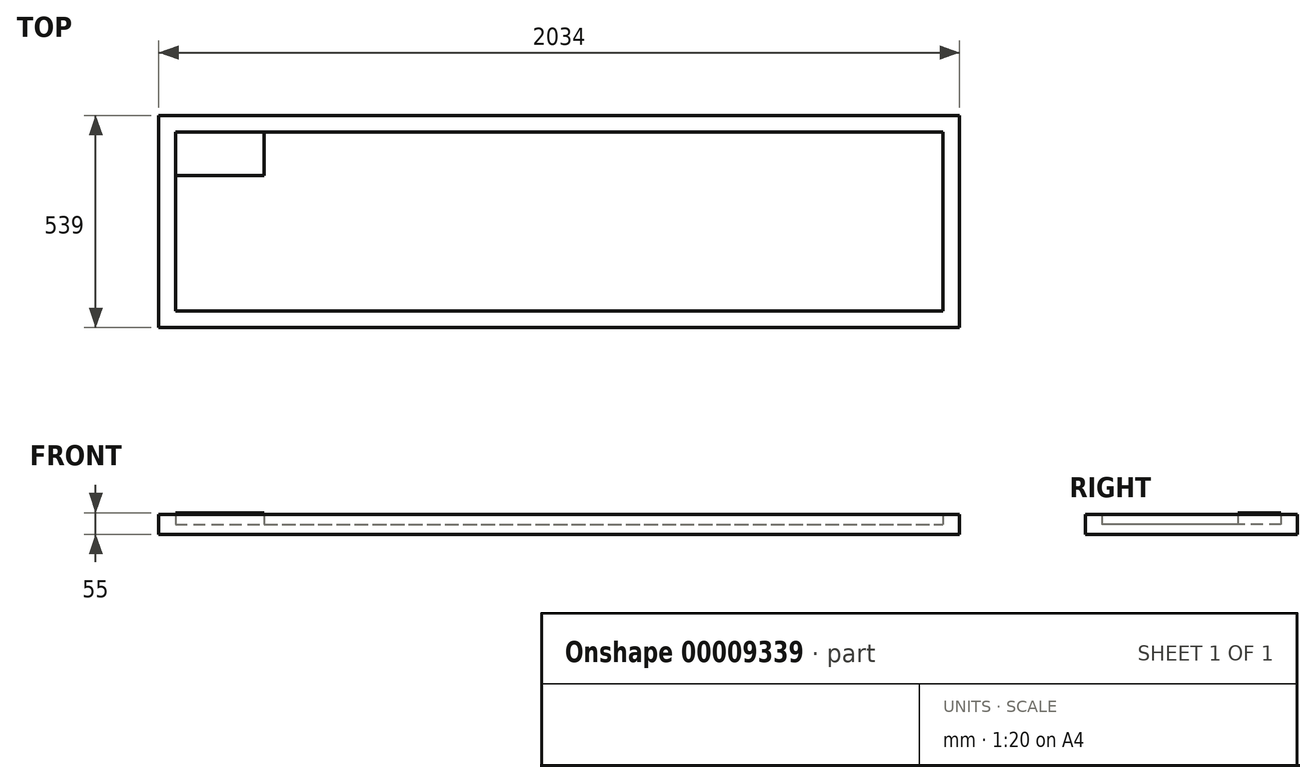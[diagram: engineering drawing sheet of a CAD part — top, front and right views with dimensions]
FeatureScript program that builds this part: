
annotation { "Feature Type Name" : "Feature", "Feature Type Description" : "" }
export const myFeature = defineFeature(function(context is Context, id is Id, definition is map)
    precondition{}
    {
        {
            var Q0;
            Q0=qCreatedBy(makeId("Top.planeOp"),FACE);
            var sketch = newSketch(context, id + "F0", { "sketchPlane" : qUnion([Q0])});
            skLineSegment(sketch, "E0", {"start": v(0, 0) * mm, "end": v(45, 0) * mm});
            skLineSegment(sketch, "E1", {"start": v(45, 0) * mm, "end": v(45, 5) * mm});
            skLineSegment(sketch, "E2", {"start": v(45, 5) * mm, "end": v(25, 5) * mm});
            skLineSegment(sketch, "E3", {"start": v(25, 5) * mm, "end": v(25, 25) * mm});
            skLineSegment(sketch, "E4", {"start": v(25, 25) * mm, "end": v(20, 25) * mm});
            skLineSegment(sketch, "E5", {"start": v(20, 25) * mm, "end": v(20, 5) * mm});
            skLineSegment(sketch, "E6", {"start": v(20, 5) * mm, "end": v(0, 5) * mm});
            skLineSegment(sketch, "E7", {"start": v(0, 5) * mm, "end": v(0, 0) * mm});
            skSolve(sketch);
        }
        {
            var Q0;
            Q0=makeQuery(id+"F0.imprint","IMPRINT",FACE,{"disambiguationData":[TD([[makeQuery(id+"F0.imprint","IMPRINT",EDGE,{"derivedFrom":sQuery(id+"F0.wireOp",EDGE,"E0")}),1.0]])]});
            extrude(context, id + "F1", {"entities" : qUnion([Q0]), "depth" : 8 * mm});
        }
        {
            var Q0;
            Q0=qCreatedBy(makeId("Top.planeOp"),FACE);
            var sketch = newSketch(context, id + "F2", { "sketchPlane" : qUnion([Q0])});
            skLineSegment(sketch, "E8.bottom", {"start": v(0, 0) * mm, "end": v(225, 0) * mm});
            skLineSegment(sketch, "E8.top", {"start": v(0, -110) * mm, "end": v(225, -110) * mm});
            skLineSegment(sketch, "E8.left", {"start": v(0, 0) * mm, "end": v(0, -110) * mm});
            skLineSegment(sketch, "E8.right", {"start": v(225, 0) * mm, "end": v(225, -110) * mm});
            skSolve(sketch);
        }
        {
            var Q0;
            Q0=makeQuery(id+"F2.imprint","IMPRINT",FACE,{"disambiguationData":[TD([[makeQuery(id+"F2.imprint","IMPRINT",EDGE,{"derivedFrom":sQuery(id+"F2.wireOp",EDGE,"E8.bottom")}),-1.0]])]});
            extrude(context, id + "F3", {"entities" : qUnion([Q0]), "depth" : 30 * mm});
        }
        {
            var Q0;
            Q0=qCreatedBy(makeId("Top.planeOp"),FACE);
            var sketch = newSketch(context, id + "F4", { "sketchPlane" : qUnion([Q0])});
            skLineSegment(sketch, "E9.bottom", {"start": v(0, 0) * mm, "end": v(1950, 0) * mm});
            skLineSegment(sketch, "E9.top", {"start": v(0, -455) * mm, "end": v(1950, -455) * mm});
            skLineSegment(sketch, "E9.left", {"start": v(0, 0) * mm, "end": v(0, -455) * mm});
            skLineSegment(sketch, "E9.right", {"start": v(1950, 0) * mm, "end": v(1950, -455) * mm});
            skLineSegment(sketch, "E10.bottom", {"start": v(1992, -497) * mm, "end": v(-42, -497) * mm});
            skLineSegment(sketch, "E10.top", {"start": v(1992, 42) * mm, "end": v(-42, 42) * mm});
            skLineSegment(sketch, "E10.left", {"start": v(1992, -497) * mm, "end": v(1992, 42) * mm});
            skLineSegment(sketch, "E10.right", {"start": v(-42, -497) * mm, "end": v(-42, 42) * mm});
            skSolve(sketch);
        }
        {
            var Q0;
            Q0=makeQuery(id+"F4.imprint","IMPRINT",FACE,{"disambiguationData":[TD([[makeQuery(id+"F4.imprint","IMPRINT",EDGE,{"derivedFrom":sQuery(id+"F4.wireOp",EDGE,"E9.bottom")}),1.0]])]});
            var Q1;
            Q1=makeQuery(id+"F4.imprint","IMPRINT",FACE,{"disambiguationData":[TD([[makeQuery(id+"F4.imprint","IMPRINT",EDGE,{"derivedFrom":sQuery(id+"F4.wireOp",EDGE,"E9.bottom")}),-1.0]])]});
            extrude(context, id + "F5", {"entities" : qUnion([Q0, Q1]), "oppositeDirection" : true, "depth" : 25 * mm});
        }
        {
            var Q0;
            Q0=makeQuery(id+"F4.imprint","IMPRINT",FACE,{"disambiguationData":[TD([[makeQuery(id+"F4.imprint","IMPRINT",EDGE,{"derivedFrom":sQuery(id+"F4.wireOp",EDGE,"E9.bottom")}),1.0]])]});
            extrude(context, id + "F6", {"entities" : qUnion([Q0]), "operationType" : NewBodyOperationType.ADD, "depth" : 25 * mm});
        }
    });
